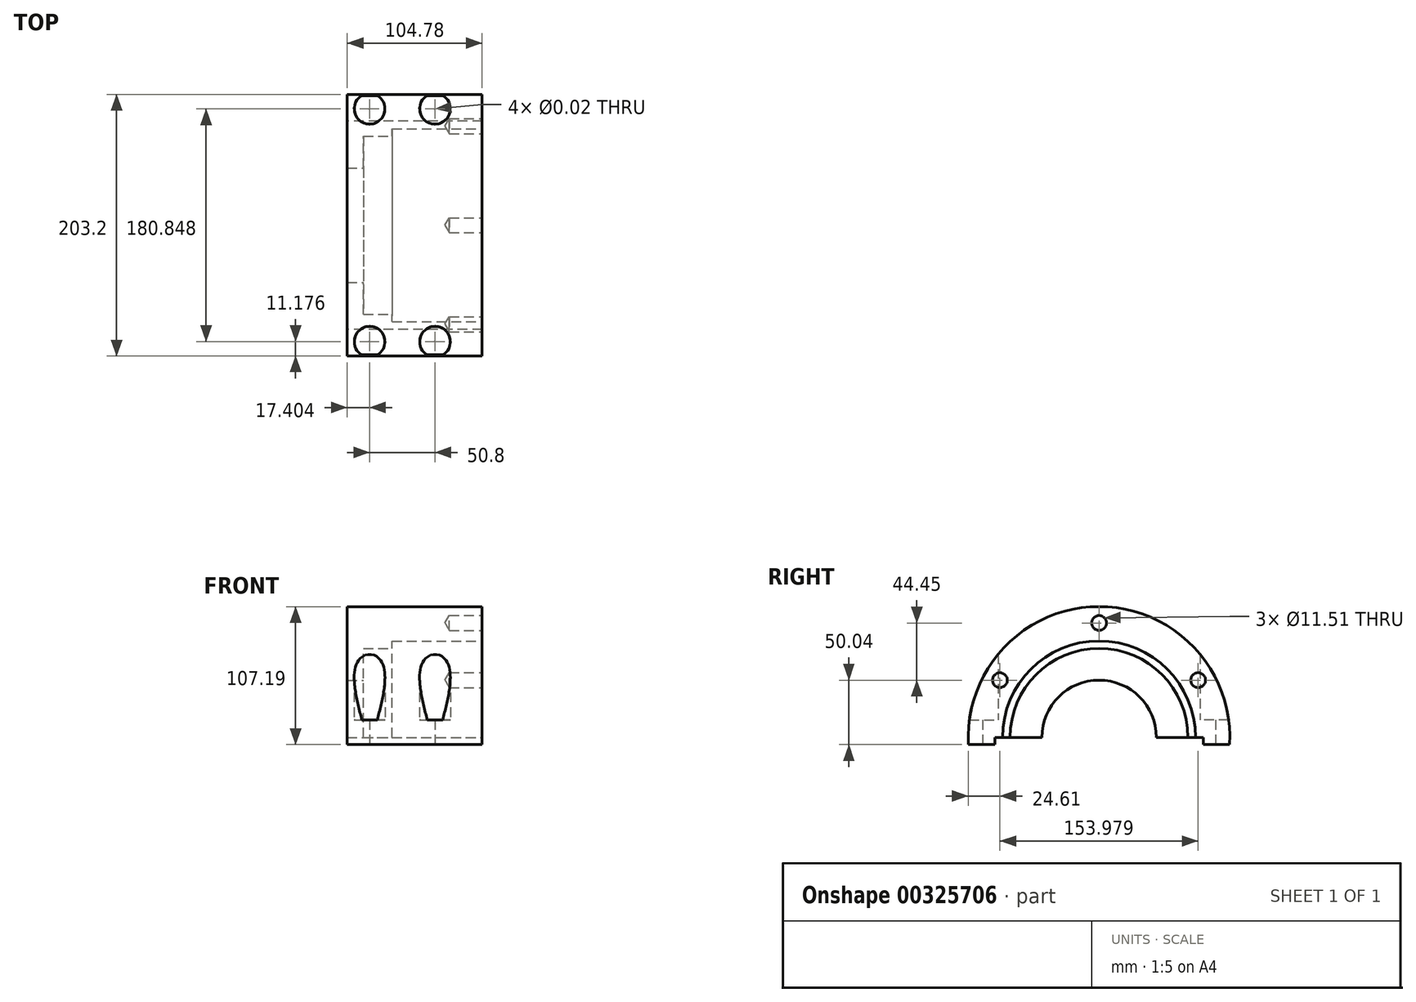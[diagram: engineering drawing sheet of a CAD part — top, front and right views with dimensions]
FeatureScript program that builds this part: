
annotation { "Feature Type Name" : "Feature", "Feature Type Description" : "" }
export const myFeature = defineFeature(function(context is Context, id is Id, definition is map)
    precondition{}
    {
        {
            var Q0;
            Q0=qCreatedBy(makeId("Right.planeOp"),FACE);
            var sketch = newSketch(context, id + "F0", { "sketchPlane" : qUnion([Q0])});
            skCircle(sketch, "E0", {"center": v(0, 0) * mm, "radius": 101.6 * mm});
            skSolve(sketch);
        }
        {
            var Q0;
            Q0=qSketchRegion(id+"F0",true);
            extrude(context, id + "F1", {"entities" : qUnion([Q0]), "oppositeDirection" : true, "depth" : 104.77 * mm});
        }
        {
            var Q0;
            Q0=makeQuery(id+"F1.opExtrude","CAP_FACE",FACE,{"disambiguationData":[OSD([sQuery(id+"F0.wireOp",EDGE,"E0")])],"isStart":true});
            var sketch = newSketch(context, id + "F2", { "sketchPlane" : qUnion([Q0])});
            skPoint(sketch, "E1", {"position": v(0, 0) * mm});
            skSolve(sketch);
        }
        {
            var Q0;
            Q0=sQuery(id+"F2.wireOp",VERTEX,"E1");
            var Q1;
            Q1=makeQuery(id+"F1.opExtrude","SWEPT_BODY",BODY,{"disambiguationData":[OSD([sQuery(id+"F0.wireOp",EDGE,"E0")])]});
            hole(context, id + "F3", {"style" : HoleStyle.C_BORE, "endStyle" : HoleEndStyle.THROUGH, "holeDiameter" : 88.9 * mm, "cBoreDiameter" : 138.18 * mm, "cBoreDepth" : 92.07 * mm, "tappedDepth" : 25.9 * mm, "tapClearance" : 3, "locations" : qUnion([Q0]), "scope" : qUnion([Q1])});
        }
        {
            var Q0;
            Q0=makeQuery(id+"F1.opExtrude","CAP_FACE",FACE,{"disambiguationData":[OSD([sQuery(id+"F0.wireOp",EDGE,"E0")])],"isStart":true});
            var sketch = newSketch(context, id + "F4", { "sketchPlane" : qUnion([Q0])});
            skCircle(sketch, "E2", {"center": v(0, 0) * mm, "radius": 74.93 * mm});
            skSolve(sketch);
        }
        {
            var Q0;
            Q0=qSketchRegion(id+"F4",true);
            extrude(context, id + "F5", {"entities" : qUnion([Q0]), "operationType" : NewBodyOperationType.REMOVE, "oppositeDirection" : true, "depth" : 69.85 * mm});
        }
        {
            var Q0;
            Q0=makeQuery(id+"F1.opExtrude","CAP_FACE",FACE,{"disambiguationData":[OSD([sQuery(id+"F0.wireOp",EDGE,"E0")])],"isStart":true});
            var sketch = newSketch(context, id + "F6", { "sketchPlane" : qUnion([Q0])});
            skLineSegment(sketch, "E3", {"start": v(-134.97, 0) * mm, "end": v(144.4, 0) * mm, "construction": true});
            skLineSegment(sketch, "E4.0", {"start": v(-134.97, -5.59) * mm, "end": v(144.4, -5.59) * mm, "construction": true});
            skLineSegment(sketch, "E5.bottom", {"start": v(-134.97, -5.59) * mm, "end": v(153.54, -5.59) * mm});
            skLineSegment(sketch, "E5.top", {"start": v(-134.97, -103.44) * mm, "end": v(153.54, -103.44) * mm});
            skLineSegment(sketch, "E5.left", {"start": v(-134.97, -5.59) * mm, "end": v(-134.97, -103.44) * mm});
            skLineSegment(sketch, "E5.right", {"start": v(153.54, -5.59) * mm, "end": v(153.54, -103.44) * mm});
            skSolve(sketch);
        }
        {
            var Q0;
            Q0=qSketchRegion(id+"F6",true);
            extrude(context, id + "F7", {"entities" : qUnion([Q0]), "operationType" : NewBodyOperationType.REMOVE, "endBound" : BoundingType.THROUGH_ALL, "oppositeDirection" : true, "depth" : 25.4 * mm});
        }
        {
            var Q0;
            Q0=makeQuery(id+"F1.opExtrude","CAP_FACE",FACE,{"disambiguationData":[OSD([sQuery(id+"F0.wireOp",EDGE,"E0")])],"isStart":true});
            var sketch = newSketch(context, id + "F8", { "sketchPlane" : qUnion([Q0])});
            skLineSegment(sketch, "E6", {"start": v(-144.4, 0) * mm, "end": v(151.77, 0) * mm, "construction": true});
            skLineSegment(sketch, "E7", {"start": v(0, 119.91) * mm, "end": v(0, -39.22) * mm, "construction": true});
            skLineSegment(sketch, "E8.0", {"start": v(-80.96, 119.91) * mm, "end": v(-80.96, -39.22) * mm, "construction": true});
            skLineSegment(sketch, "E9.bottom", {"start": v(-80.96, 0) * mm, "end": v(0, 0) * mm});
            skLineSegment(sketch, "E9.top", {"start": v(-80.96, -28.03) * mm, "end": v(0, -28.03) * mm});
            skLineSegment(sketch, "E9.left", {"start": v(-80.96, 0) * mm, "end": v(-80.96, -28.03) * mm});
            skLineSegment(sketch, "E9.right", {"start": v(0, 0) * mm, "end": v(0, -28.03) * mm});
            skLineSegment(sketch, "E10.MirrorCS", {"start": v(80.96, 0) * mm, "end": v(80.96, -28.03) * mm});
            skLineSegment(sketch, "E11.MirrorCS", {"start": v(80.96, -28.03) * mm, "end": v(0, -28.03) * mm});
            skLineSegment(sketch, "E12.MirrorCS", {"start": v(80.96, 0) * mm, "end": v(0, 0) * mm});
            skSolve(sketch);
        }
        {
            var Q0;
            Q0=qSketchRegion(id+"F8",true);
            extrude(context, id + "F9", {"entities" : qUnion([Q0]), "operationType" : NewBodyOperationType.REMOVE, "endBound" : BoundingType.THROUGH_ALL, "oppositeDirection" : true, "depth" : 25.4 * mm});
        }
        {
            var Q0;
            Q0=makeQuery(id+"F7.boolean.opBoolean","COPY",FACE,{"disambiguationData":[OD(0.0)],"derivedFrom":makeQuery(id+"F7.opExtrude","SWEPT_FACE",FACE,{"disambiguationData":[OSD([sQuery(id+"F6.wireOp",EDGE,"E5.bottom")])]})});
            var sketch = newSketch(context, id + "F10", { "sketchPlane" : qUnion([Q0])});
            skLineSegment(sketch, "E13", {"start": v(48.99, 0) * mm, "end": v(-129.6, 0) * mm, "construction": true});
            skLineSegment(sketch, "E14.0", {"start": v(0, 101.45) * mm, "end": v(0, 80.96) * mm, "construction": true});
            skLineSegment(sketch, "E15.0", {"start": v(48.99, 90.42) * mm, "end": v(-129.6, 90.42) * mm, "construction": true});
            skLineSegment(sketch, "E16.0", {"start": v(-36.58, 101.45) * mm, "end": v(-36.58, 80.96) * mm, "construction": true});
            skLineSegment(sketch, "E17.0", {"start": v(-87.38, 101.45) * mm, "end": v(-87.38, 80.96) * mm, "construction": true});
            skPoint(sketch, "E18", {"position": v(-36.58, 90.42) * mm});
            skPoint(sketch, "E19", {"position": v(-87.38, 90.42) * mm});
            skPoint(sketch, "E20.MirrorP", {"position": v(-36.58, -90.42) * mm});
            skPoint(sketch, "E21.MirrorP", {"position": v(-87.38, -90.42) * mm});
            skSolve(sketch);
        }
        {
            var Q0;
            Q0=sQuery(id+"F10.wireOp",VERTEX,"E18");
            var Q1;
            Q1=sQuery(id+"F10.wireOp",VERTEX,"E19");
            var Q2;
            Q2=sQuery(id+"F10.wireOp",VERTEX,"E20.MirrorP");
            var Q3;
            Q3=sQuery(id+"F10.wireOp",VERTEX,"E21.MirrorP");
            var Q4;
            Q4=makeQuery(id+"F1.opExtrude","SWEPT_BODY",BODY,{"disambiguationData":[OSD([sQuery(id+"F0.wireOp",EDGE,"E0")])]});
            hole(context, id + "F11", {"style" : HoleStyle.SIMPLE, "endStyle" : HoleEndStyle.THROUGH, "standardTappedOrClearance" : lookupTablePath({ "standard" : "ANSI", "size" : "9/16 (0.56)", "type" : "Drilled" }), "standardBlindInLast" : lookupTablePath({ "standard" : "ANSI", "size" : "9/16", "type" : "Drilled" }), "holeDiameter" : 9 / 406.4 * mm, "tappedDepth" : 25.88 * mm, "tapClearance" : 3, "locations" : qUnion([Q0, Q1, Q2, Q3]), "scope" : qUnion([Q4])});
        }
        {
            var Q0;
            Q0=makeQuery(id+"F7.boolean.opBoolean","COPY",FACE,{"disambiguationData":[OD(0.0)],"derivedFrom":makeQuery(id+"F7.opExtrude","SWEPT_FACE",FACE,{"disambiguationData":[OSD([sQuery(id+"F6.wireOp",EDGE,"E5.bottom")])]})});
            cPlane(context, id + "F12", {"entities" : qUnion([Q0]), "cplaneType" : CPlaneType.OFFSET, "offset" : 19.05 * mm, "oppositeDirection" : true, "width" : 152.4 * mm, "height" : 152.4 * mm});
        }
        {
            var Q0;
            Q0=qCreatedBy(id+"F12.planeOp",FACE);
            var sketch = newSketch(context, id + "F13", { "sketchPlane" : qUnion([Q0])});
            skCircle(sketch, "E22.0", {"center": v(-87.38, 90.42) * mm, "radius": 7.14 * mm, "construction": true});
            skCircle(sketch, "E23.0", {"center": v(-36.58, 90.42) * mm, "radius": 7.14 * mm, "construction": true});
            skCircle(sketch, "E24.0", {"center": v(-87.38, -90.42) * mm, "radius": 7.14 * mm, "construction": true});
            skCircle(sketch, "E25.0", {"center": v(-36.58, -90.42) * mm, "radius": 7.14 * mm, "construction": true});
            skLineSegment(sketch, "E26.0", {"start": v(-104.78, 101.6) * mm, "end": v(-104.78, -101.6) * mm, "construction": true});
            skLineSegment(sketch, "E27", {"start": v(101.37, 0) * mm, "end": v(-145.5, 0) * mm, "construction": true});
            skCircle(sketch, "E28", {"center": v(-87.38, 90.42) * mm, "radius": 11.94 * mm});
            skCircle(sketch, "E29", {"center": v(-36.58, 90.42) * mm, "radius": 11.94 * mm});
            skCircle(sketch, "E30.MirrorC", {"center": v(-87.38, -90.42) * mm, "radius": 11.94 * mm});
            skCircle(sketch, "E31.MirrorC", {"center": v(-36.58, -90.42) * mm, "radius": 11.94 * mm});
            skSolve(sketch);
        }
        {
            var Q0;
            Q0=qSketchRegion(id+"F13",true);
            extrude(context, id + "F14", {"entities" : qUnion([Q0]), "operationType" : NewBodyOperationType.REMOVE, "endBound" : BoundingType.THROUGH_ALL, "oppositeDirection" : true, "depth" : 25.4 * mm});
        }
        {
            var Q0;
            Q0=makeQuery(id+"F1.opExtrude","CAP_FACE",FACE,{"disambiguationData":[OSD([sQuery(id+"F0.wireOp",EDGE,"E0")])],"isStart":true});
            var sketch = newSketch(context, id + "F15", { "sketchPlane" : qUnion([Q0])});
            skLineSegment(sketch, "E32", {"start": v(0, 0) * mm, "end": v(0, 141.98) * mm, "construction": true});
            skLineSegment(sketch, "E33", {"start": v(0, 0) * mm, "end": v(-175.98, 101.6) * mm, "construction": true});
            skPoint(sketch, "E33.endSnap0", {"position": v(0, 101.6) * mm});
            skCircle(sketch, "E34", {"center": v(0, 0) * mm, "radius": 88.9 * mm, "construction": true});
            skPoint(sketch, "E35", {"position": v(-76.99, 44.45) * mm});
            skPoint(sketch, "E36", {"position": v(0, 88.9) * mm});
            skPoint(sketch, "E37.MirrorP", {"position": v(76.99, 44.45) * mm});
            skSolve(sketch);
        }
        {
            var Q0;
            Q0=sQuery(id+"F15.wireOp",VERTEX,"E35");
            var Q1;
            Q1=sQuery(id+"F15.wireOp",VERTEX,"E36");
            var Q2;
            Q2=sQuery(id+"F15.wireOp",VERTEX,"E37.MirrorP");
            var Q3;
            Q3=makeQuery(id+"F1.opExtrude","SWEPT_BODY",BODY,{"disambiguationData":[OSD([sQuery(id+"F0.wireOp",EDGE,"E0")])]});
            hole(context, id + "F16", {"style" : HoleStyle.SIMPLE, "endStyle" : HoleEndStyle.BLIND, "standardTappedOrClearance" : lookupTablePath({ "standard" : "ANSI", "engagement" : "75%", "pitch" : "20 tpi", "size" : "1/2", "type" : "Tapped" }), "standardBlindInLast" : lookupTablePath({ "standard" : "ANSI", "engagement" : "75%", "pitch" : "20 tpi", "size" : "1/2", "type" : "Tapped" }), "holeDiameter" : 11.5 * mm, "showTappedDepth" : true, "holeDepth" : 25.4 * mm, "tappedDepth" : 21.59 * mm, "tapClearance" : 3, "locations" : qUnion([Q0, Q1, Q2]), "scope" : qUnion([Q3]), "majorDiameter" : 12.7 * mm});
        }
    });
